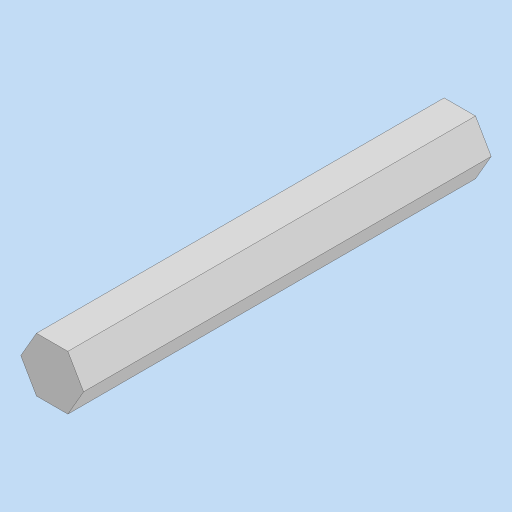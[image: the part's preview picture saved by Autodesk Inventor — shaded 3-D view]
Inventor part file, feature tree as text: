
AUTODESK INVENTOR PART (.ipt)
format: ipt  version: 2023 (Build 270158000, 158)  size: 82,944 bytes
history: native  units: in
note: dims shown in document units (in); Inventor stores cm internally (conversion verified against a paired STEP export)
features: extrude x1, sketch x1
ambient origin geometry x8: Origin, YZ Plane, XZ Plane, XY Plane, X Axis, Y Axis, Z Axis, Center Point
bodies: Solid1 (feature_tree)
feature tree (2):
  extrude  "Extrusion1"  Depth=3.75in TaperAngle=0.0deg
  sketch  "Sketch1"  dims[d0=0.5in d1=3.75in d2=0.0in]
